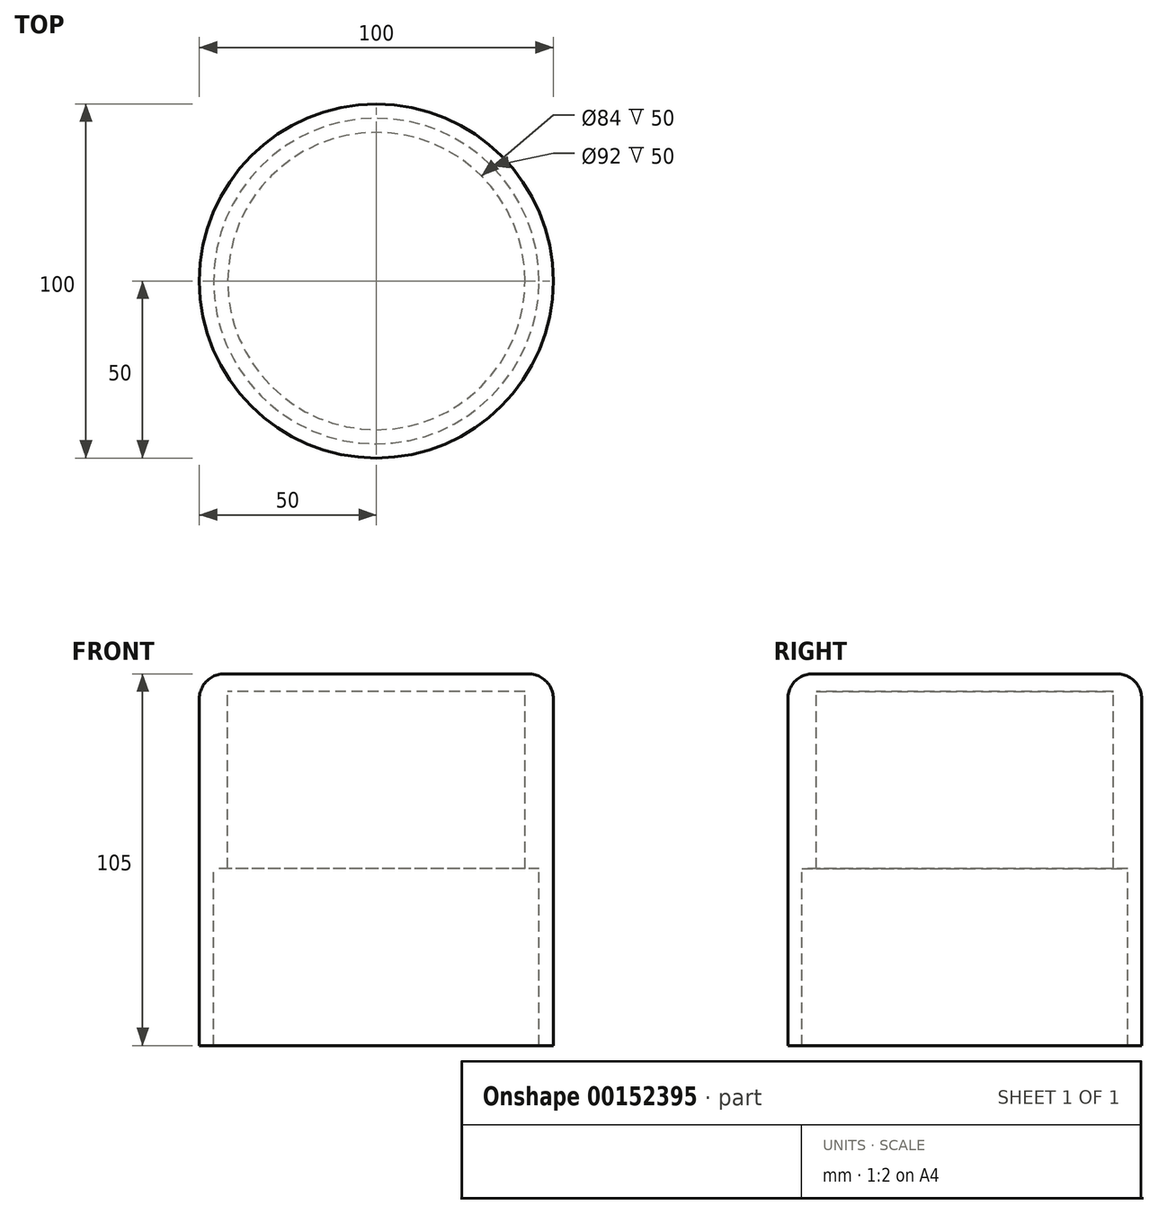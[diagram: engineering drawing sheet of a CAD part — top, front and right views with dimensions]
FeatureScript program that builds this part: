
annotation { "Feature Type Name" : "Feature", "Feature Type Description" : "" }
export const myFeature = defineFeature(function(context is Context, id is Id, definition is map)
    precondition{}
    {
        {
            var Q0;
            Q0=qCreatedBy(makeId("Top.planeOp"),FACE);
            var sketch = newSketch(context, id + "F0", { "sketchPlane" : qUnion([Q0])});
            skCircle(sketch, "E0", {"center": v(0, 0) * mm, "radius": 42 * mm});
            skCircle(sketch, "E1", {"center": v(0, 0) * mm, "radius": 46 * mm});
            skCircle(sketch, "E2", {"center": v(0, 0) * mm, "radius": 50 * mm});
            skSolve(sketch);
        }
        {
            var Q0;
            Q0 = qSketchRegion(id + "F0", true);
            var Q1;
            Q1=makeQuery(id+"F0.imprint","IMPRINT",FACE,{"disambiguationData":[TD([[makeQuery(id+"F0.imprint","IMPRINT",EDGE,{"derivedFrom":sQuery(id+"F0.wireOp",EDGE,"E0")}),-1.0]])]});
            var Q2;
            Q2=makeQuery(id+"F0.imprint","IMPRINT",FACE,{"disambiguationData":[TD([[makeQuery(id+"F0.imprint","IMPRINT",EDGE,{"derivedFrom":sQuery(id+"F0.wireOp",EDGE,"E0")}),1.0]])]});
            extrude(context, id + "F1", {"entities" : qUnion([Q0, Q1, Q2]), "depth" : 5 * mm});
        }
        {
            var Q0;
            Q0=makeQuery(id+"F0.imprint","IMPRINT",FACE,{"disambiguationData":[TD([[makeQuery(id+"F0.imprint","IMPRINT",EDGE,{"derivedFrom":sQuery(id+"F0.wireOp",EDGE,"E0")}),-1.0]])]});
            extrude(context, id + "F2", {"entities" : qUnion([Q0]), "operationType" : NewBodyOperationType.ADD, "oppositeDirection" : true, "depth" : 50 * mm});
        }
        {
            var Q0;
            Q0=makeQuery(id+"F0.imprint","IMPRINT",FACE,{"disambiguationData":[TD([[makeQuery(id+"F0.imprint","IMPRINT",EDGE,{"derivedFrom":sQuery(id+"F0.wireOp",EDGE,"E1")}),-1.0]])]});
            extrude(context, id + "F3", {"entities" : qUnion([Q0]), "operationType" : NewBodyOperationType.ADD, "oppositeDirection" : true, "depth" : 100 * mm});
        }
        {
            var Q0;
            Q0=makeQuery(id+"F1.opExtrude","CAP_EDGE",EDGE,{"disambiguationData":[OSD([sQuery(id+"F0.wireOp",EDGE,"E2")])],"isStart":false});
            fillet(context, id + "F4", {"entities" : qUnion([Q0]), "radius" : 7 * mm, "tangentPropagation" : true, "allowEdgeOverflow" : false});
        }
    });
